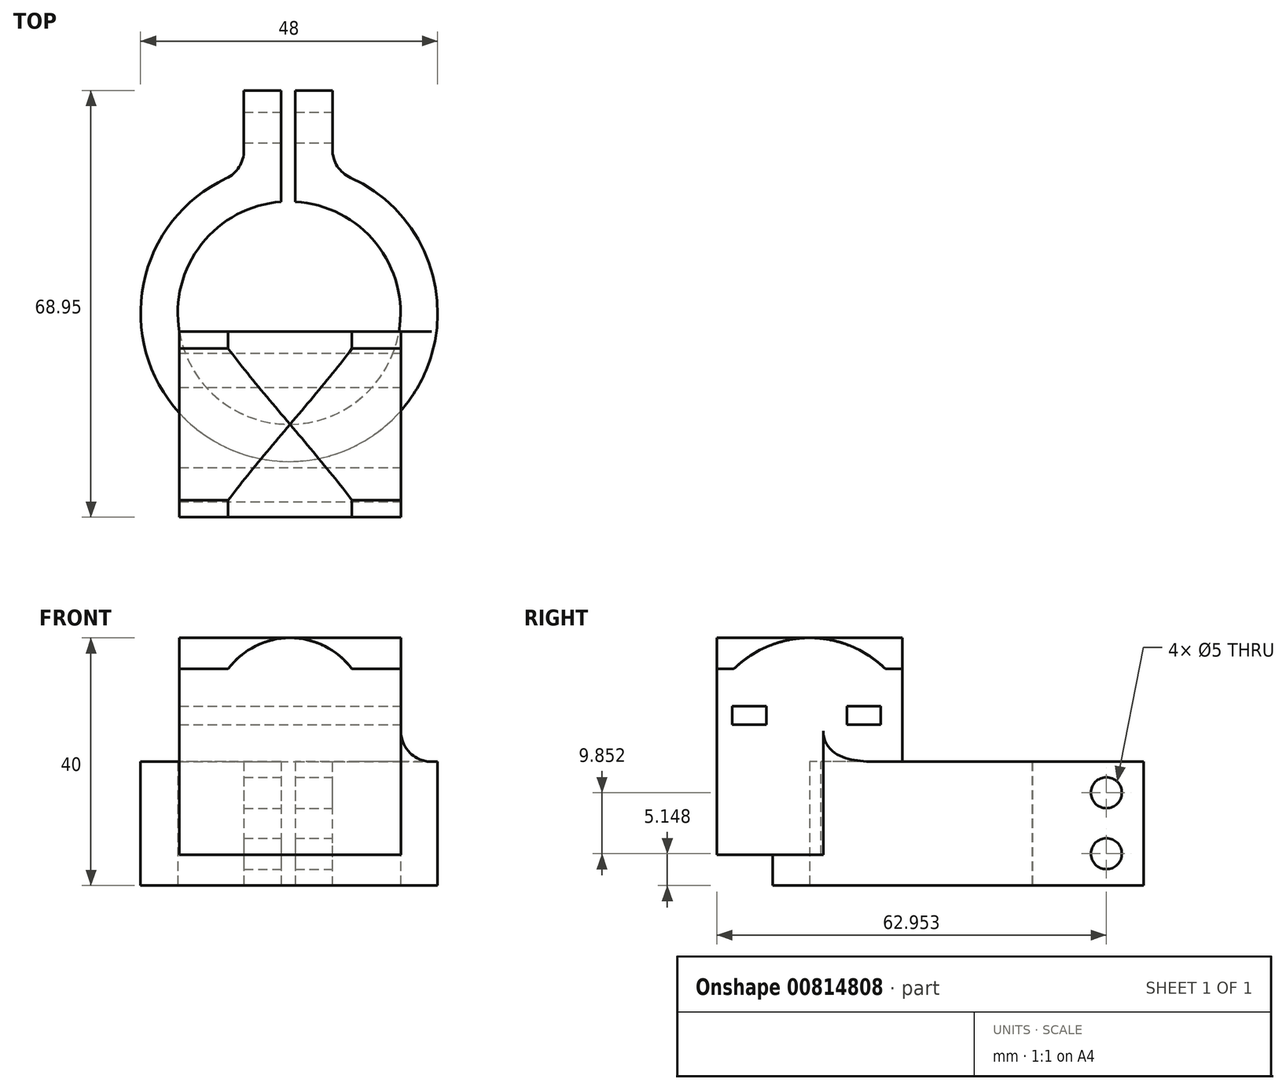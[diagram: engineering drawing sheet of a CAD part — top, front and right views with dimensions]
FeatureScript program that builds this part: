
annotation { "Feature Type Name" : "Feature", "Feature Type Description" : "" }
export const myFeature = defineFeature(function(context is Context, id is Id, definition is map)
    precondition{}
    {
        {
            var Q0;
            Q0=qCreatedBy(makeId("Top.planeOp"),FACE);
            var sketch = newSketch(context, id + "F0", { "sketchPlane" : qUnion([Q0])});
            skArc(sketch, "E0", {"start": v(-1.3, 17.95) * mm, "mid": v(0.15, -18) * mm, "end": v(1, 17.97) * mm});
            skLineSegment(sketch, "E1", {"start": v(-1.3, 17.95) * mm, "end": v(-1.3, 35.95) * mm});
            skLineSegment(sketch, "E2", {"start": v(1, 17.97) * mm, "end": v(1, 35.95) * mm});
            skLineSegment(sketch, "E3.0", {"start": v(7, 22.96) * mm, "end": v(7, 35.95) * mm});
            skArc(sketch, "E3.1", {"start": v(-7.3, 22.86) * mm, "mid": v(0.16, -24) * mm, "end": v(7, 22.96) * mm});
            skLineSegment(sketch, "E3.2", {"start": v(-7.3, 22.86) * mm, "end": v(-7.3, 35.95) * mm});
            skLineSegment(sketch, "E4", {"start": v(-7.3, 35.95) * mm, "end": v(-1.3, 35.95) * mm});
            skLineSegment(sketch, "E5", {"start": v(1, 35.95) * mm, "end": v(7, 35.95) * mm});
            skSolve(sketch);
        }
        {
            var Q0;
            Q0=makeQuery(id+"F0.imprint","IMPRINT",FACE,{"disambiguationData":[TD([[makeQuery(id+"F0.imprint","IMPRINT",EDGE,{"derivedFrom":sQuery(id+"F0.wireOp",EDGE,"E0")}),-1.0]])]});
            extrude(context, id + "F1", {"entities" : qUnion([Q0]), "depth" : 20 * mm, "offsetDistance" : 25 * mm});
        }
        {
            var Q0;
            Q0=makeQuery(id+"F1.opExtrude","SWEPT_EDGE",EDGE,{"disambiguationData":[OSD([sQuery(id+"F0.wireOp",EDGE,"E3.0"),sQuery(id+"F0.wireOp",EDGE,"E3.1")])]});
            var Q1;
            Q1=makeQuery(id+"F1.opExtrude","SWEPT_EDGE",EDGE,{"disambiguationData":[OSD([sQuery(id+"F0.wireOp",EDGE,"E3.1"),sQuery(id+"F0.wireOp",EDGE,"E3.2")])]});
            fillet(context, id + "F2", {"entities" : qUnion([Q0, Q1]), "radius" : 5 * mm, "tangentPropagation" : true, "allowEdgeOverflow" : false});
        }
        {
            var Q0;
            Q0=makeQuery(id+"F1.opExtrude","SWEPT_FACE",FACE,{"disambiguationData":[OSD([sQuery(id+"F0.wireOp",EDGE,"E3.0")])]});
            var sketch = newSketch(context, id + "F3", { "sketchPlane" : qUnion([Q0])});
            skCircle(sketch, "E6", {"center": v(29.95, 15) * mm, "radius": 2.5 * mm});
            skCircle(sketch, "E7", {"center": v(29.95, 5.15) * mm, "radius": 2.5 * mm});
            skSolve(sketch);
        }
        {
            var Q0;
            Q0=makeQuery(id+"F3.imprint","IMPRINT",FACE,{"disambiguationData":[TD([[makeQuery(id+"F3.imprint","IMPRINT",EDGE,{"derivedFrom":sQuery(id+"F3.wireOp",EDGE,"E6")}),1.0]])]});
            var Q1;
            Q1=makeQuery(id+"F3.imprint","IMPRINT",FACE,{"disambiguationData":[TD([[makeQuery(id+"F3.imprint","IMPRINT",EDGE,{"derivedFrom":sQuery(id+"F3.wireOp",EDGE,"E7")}),1.0]])]});
            extrude(context, id + "F4", {"entities" : qUnion([Q0, Q1]), "operationType" : NewBodyOperationType.REMOVE, "oppositeDirection" : true, "depth" : 25 * mm, "offsetDistance" : 25 * mm});
        }
        {
            var Q0;
            Q0=makeQuery(id+"F1.opExtrude","CAP_FACE",FACE,{"disambiguationData":[OSD([sQuery(id+"F0.wireOp",EDGE,"E0"),sQuery(id+"F0.wireOp",EDGE,"E1"),sQuery(id+"F0.wireOp",EDGE,"E2"),sQuery(id+"F0.wireOp",EDGE,"E3.0"),sQuery(id+"F0.wireOp",EDGE,"E3.1"),sQuery(id+"F0.wireOp",EDGE,"E3.2"),sQuery(id+"F0.wireOp",EDGE,"E4"),sQuery(id+"F0.wireOp",EDGE,"E5")])],"isStart":false});
            var sketch = newSketch(context, id + "F5", { "sketchPlane" : qUnion([Q0])});
            skPoint(sketch, "E8.middle", {"position": v(0, 0) * mm});
            skLineSegment(sketch, "E9", {"start": v(-30.55, 0) * mm, "end": v(33.82, 0) * mm, "construction": true});
            skLineSegment(sketch, "E10.bottom", {"start": v(-17.75, -3) * mm, "end": v(18.05, -3) * mm});
            skLineSegment(sketch, "E10.top", {"start": v(-17.75, -33) * mm, "end": v(18.05, -33) * mm});
            skLineSegment(sketch, "E10.left", {"start": v(-17.75, -3) * mm, "end": v(-17.75, -33) * mm});
            skLineSegment(sketch, "E10.right", {"start": v(18.05, -3) * mm, "end": v(18.05, -33) * mm});
            skPoint(sketch, "E10.middle", {"position": v(0.15, -18) * mm});
            skLineSegment(sketch, "E11", {"start": v(0, 0) * mm, "end": v(0, -35.02) * mm, "construction": true});
            skSolve(sketch);
        }
        {
            var Q0;
            {var subQ0=sQuery(id+"F5.wireOp",EDGE,"E10.left");var subQ4=makeQuery(id+"F1.opExtrude","CAP_EDGE",EDGE,{"disambiguationData":[OSD([sQuery(id+"F0.wireOp",EDGE,"E3.1")])],"isStart":false});var subQ5=makeQuery(id+"F5.imprint","INTERSECT",VERTEX,{"derivedFrom":[subQ4,subQ0]});Q0=makeQuery(id+"F5.imprint","IMPRINT",FACE,{"disambiguationData":[TD([[makeQuery(id+"F5.imprint","IMPRINT",EDGE,{"disambiguationData":[TD([[subQ5,-1.0]])],"derivedFrom":subQ4}),1.0]])]});}
            var Q1;
            {var subQ0=sQuery(id+"F5.wireOp",EDGE,"E10.top");Q1=makeQuery(id+"F5.imprint","IMPRINT",FACE,{"disambiguationData":[TD([[makeQuery(id+"F5.imprint","IMPRINT",EDGE,{"derivedFrom":subQ0}),1.0]])]});}
            var Q2;
            {var subQ0=sQuery(id+"F5.wireOp",EDGE,"E10.bottom");Q2=makeQuery(id+"F5.imprint","IMPRINT",FACE,{"disambiguationData":[TD([[makeQuery(id+"F5.imprint","IMPRINT",EDGE,{"derivedFrom":subQ0}),-1.0]])]});}
            extrude(context, id + "F6", {"entities" : qUnion([Q0, Q1, Q2]), "operationType" : NewBodyOperationType.ADD, "depth" : 15 * mm, "offsetDistance" : 25 * mm});
        }
        {
            var Q0;
            {var subQ0=sQuery(id+"F5.wireOp",EDGE,"E10.left");var subQ1=sQuery(id+"F0.wireOp",EDGE,"E3.1");var subQ2=sQuery(id+"F5.wireOp",EDGE,"E10.top");var subQ3=sQuery(id+"F5.wireOp",EDGE,"E10.right");Q0=makeQuery(id+"F6.boolean.opBoolean","SPLIT",FACE,{"disambiguationData":[TD([makeQuery(id+"F1.opExtrude","SWEPT_FACE",FACE,{"disambiguationData":[OSD([subQ1])]})])],"derivedFrom":makeQuery(id+"F6.opExtrude","CAP_FACE",FACE,{"disambiguationData":[OSD([sQuery(id+"F5.wireOp",EDGE,"E10.bottom"),subQ2,subQ0,subQ3])],"isStart":true})});}
            extrude(context, id + "F7", {"entities" : qUnion([Q0]), "operationType" : NewBodyOperationType.ADD, "depth" : 15 * mm, "offsetDistance" : 25 * mm});
        }
        {
            var Q0;
            {var subQ0=sQuery(id+"F5.wireOp",EDGE,"E10.top");Q0=makeQuery(id+"F7.boolean.opBoolean","MERGE",FACE,{"derivedFrom":[makeQuery(id+"F6.opExtrude","SWEPT_FACE",FACE,{"disambiguationData":[OSD([subQ0])]}),makeQuery(id+"F7.opExtrude","SWEPT_FACE",FACE,{"disambiguationData":[OSD([subQ0])]})]});}
            var sketch = newSketch(context, id + "F8", { "sketchPlane" : qUnion([Q0])});
            skCircle(sketch, "E12", {"center": v(0.15, 27.5) * mm, "radius": 12.5 * mm});
            skLineSegment(sketch, "E13", {"start": v(0.15, 5) * mm, "end": v(0.15, 50) * mm, "construction": true});
            skSolve(sketch);
        }
        {
            var Q0;
            {var subQ0=sQuery(id+"F8.wireOp",EDGE,"E12");var subQ1=makeQuery(id+"F6.opExtrude","CAP_EDGE",EDGE,{"disambiguationData":[OSD([sQuery(id+"F5.wireOp",EDGE,"E10.top")])],"isStart":false});var subQ2=makeQuery(id+"F8.imprint","INTERSECT",VERTEX,{"disambiguationData":[OD(0.0)],"derivedFrom":[subQ1,subQ0]});Q0=makeQuery(id+"F8.imprint","IMPRINT",FACE,{"disambiguationData":[TD([[makeQuery(id+"F8.imprint","IMPRINT",EDGE,{"disambiguationData":[TD([[subQ2,1.0]])],"derivedFrom":subQ0}),1.0]])]});}
            extrude(context, id + "F9", {"entities" : qUnion([Q0]), "operationType" : NewBodyOperationType.ADD, "oppositeDirection" : true, "depth" : 30 * mm, "offsetDistance" : 25 * mm});
        }
        {
            var Q0;
            {var subQ0=sQuery(id+"F5.wireOp",EDGE,"E10.right");Q0=makeQuery(id+"F7.boolean.opBoolean","MERGE",FACE,{"derivedFrom":[makeQuery(id+"F6.opExtrude","SWEPT_FACE",FACE,{"disambiguationData":[OSD([subQ0])]}),makeQuery(id+"F7.opExtrude","SWEPT_FACE",FACE,{"disambiguationData":[OSD([subQ0])]})]});}
            var sketch = newSketch(context, id + "F10", { "sketchPlane" : qUnion([Q0])});
            skLineSegment(sketch, "E14", {"start": v(-18, 35) * mm, "end": v(-18, 2.36) * mm, "construction": true});
            skCircle(sketch, "E15", {"center": v(-18, 22.5) * mm, "radius": 17.5 * mm});
            skLineSegment(sketch, "E16.bottom", {"start": v(-25, 26) * mm, "end": v(-30.5, 26) * mm});
            skLineSegment(sketch, "E16.top", {"start": v(-25, 29) * mm, "end": v(-30.5, 29) * mm});
            skLineSegment(sketch, "E16.left", {"start": v(-25, 26) * mm, "end": v(-25, 29) * mm});
            skLineSegment(sketch, "E16.right", {"start": v(-30.5, 26) * mm, "end": v(-30.5, 29) * mm});
            skPoint(sketch, "E16.middle", {"position": v(-27.75, 27.5) * mm});
            skLineSegment(sketch, "E17.bottom", {"start": v(-6.5, 26) * mm, "end": v(-12, 26) * mm});
            skLineSegment(sketch, "E17.top", {"start": v(-6.5, 29) * mm, "end": v(-12, 29) * mm});
            skLineSegment(sketch, "E17.left", {"start": v(-6.5, 26) * mm, "end": v(-6.5, 29) * mm});
            skLineSegment(sketch, "E17.right", {"start": v(-12, 26) * mm, "end": v(-12, 29) * mm});
            skPoint(sketch, "E17.middle", {"position": v(-9.25, 27.5) * mm});
            skSolve(sketch);
        }
        {
            var Q0;
            {var subQ0=sQuery(id+"F10.wireOp",EDGE,"E15");var subQ1=makeQuery(id+"F6.opExtrude","CAP_EDGE",EDGE,{"disambiguationData":[OSD([sQuery(id+"F5.wireOp",EDGE,"E10.right")])],"isStart":false});var subQ2=makeQuery(id+"F10.imprint","INTERSECT",VERTEX,{"disambiguationData":[OD(0.0)],"derivedFrom":[subQ1,subQ0]});Q0=makeQuery(id+"F10.imprint","IMPRINT",FACE,{"disambiguationData":[TD([[makeQuery(id+"F10.imprint","IMPRINT",EDGE,{"disambiguationData":[TD([[subQ2,-1.0]])],"derivedFrom":subQ0}),1.0]])]});}
            extrude(context, id + "F11", {"entities" : qUnion([Q0]), "operationType" : NewBodyOperationType.ADD, "oppositeDirection" : true, "depth" : 35.8 * mm, "offsetDistance" : 25 * mm});
        }
        {
            var Q0;
            Q0=makeQuery(id+"F10.imprint","IMPRINT",FACE,{"disambiguationData":[TD([[makeQuery(id+"F10.imprint","IMPRINT",EDGE,{"derivedFrom":sQuery(id+"F10.wireOp",EDGE,"E16.bottom")}),-1.0]])]});
            var Q1;
            Q1=makeQuery(id+"F10.imprint","IMPRINT",FACE,{"disambiguationData":[TD([[makeQuery(id+"F10.imprint","IMPRINT",EDGE,{"derivedFrom":sQuery(id+"F10.wireOp",EDGE,"E17.bottom")}),-1.0]])]});
            extrude(context, id + "F12", {"entities" : qUnion([Q0, Q1]), "operationType" : NewBodyOperationType.REMOVE, "oppositeDirection" : true, "depth" : 36 * mm, "offsetDistance" : 25 * mm});
        }
        {
            var Q0;
            Q0=makeQuery(id+"F7.opExtrude","CAP_EDGE",EDGE,{"disambiguationData":[OSD([sQuery(id+"F0.wireOp",EDGE,"E3.1")])],"isStart":false});
            var Q1;
            {var subQ0=sQuery(id+"F5.wireOp",EDGE,"E10.right");var subQ1=sQuery(id+"F5.wireOp",EDGE,"E10.left");var subQ2=sQuery(id+"F5.wireOp",EDGE,"E10.top");var subQ3=sQuery(id+"F5.wireOp",EDGE,"E10.bottom");var subQ4=sQuery(id+"F0.wireOp",EDGE,"E3.1");var subQ5=sQuery(id+"F0.wireOp",EDGE,"E5");var subQ6=sQuery(id+"F0.wireOp",EDGE,"E4");var subQ7=sQuery(id+"F0.wireOp",EDGE,"E3.2");var subQ8=sQuery(id+"F0.wireOp",EDGE,"E3.0");var subQ9=sQuery(id+"F0.wireOp",EDGE,"E2");var subQ10=sQuery(id+"F0.wireOp",EDGE,"E1");var subQ11=sQuery(id+"F0.wireOp",EDGE,"E0");Q1=makeQuery(id+"F7.opExtrude","SWEPT_EDGE",EDGE,{"disambiguationData":[OSD([subQ11,subQ10,subQ9,subQ8,subQ4,subQ7,subQ6,subQ5,subQ3,subQ2,subQ1,subQ0]),TDD([makeQuery(id+"F6.boolean.opBoolean","TWEAK_VERTEX",VERTEX,{"derivedFrom":[makeQuery(id+"F1.opExtrude","CAP_FACE",FACE,{"disambiguationData":[OSD([subQ11,subQ10,subQ9,subQ8,subQ4,subQ7,subQ6,subQ5])],"isStart":false}),makeQuery(id+"F1.opExtrude","SWEPT_FACE",FACE,{"disambiguationData":[OSD([subQ4])]}),makeQuery(id+"F6.opExtrude","CAP_FACE",FACE,{"disambiguationData":[OSD([subQ3,subQ2,subQ1,subQ0])],"isStart":true}),makeQuery(id+"F6.opExtrude","SWEPT_FACE",FACE,{"disambiguationData":[OSD([subQ0])]})]})])]});}
            var Q2;
            {var subQ0=sQuery(id+"F5.wireOp",EDGE,"E10.right");Q2=makeQuery(id+"F6.boolean.opBoolean","SPLIT",EDGE,{"disambiguationData":[topologyDisambiguationEdgeConnected([makeQuery(id+"F1.opExtrude","CAP_FACE",FACE,{"disambiguationData":[OSD([sQuery(id+"F0.wireOp",EDGE,"E0"),sQuery(id+"F0.wireOp",EDGE,"E1"),sQuery(id+"F0.wireOp",EDGE,"E2"),sQuery(id+"F0.wireOp",EDGE,"E3.0"),sQuery(id+"F0.wireOp",EDGE,"E3.1"),sQuery(id+"F0.wireOp",EDGE,"E3.2"),sQuery(id+"F0.wireOp",EDGE,"E4"),sQuery(id+"F0.wireOp",EDGE,"E5")])],"isStart":false})])],"derivedFrom":makeQuery(id+"F6.opExtrude","CAP_EDGE",EDGE,{"disambiguationData":[OSD([subQ0])],"isStart":true})});}
            var Q3;
            {var subQ0=sQuery(id+"F5.wireOp",EDGE,"E10.left");Q3=makeQuery(id+"F6.boolean.opBoolean","SPLIT",EDGE,{"disambiguationData":[topologyDisambiguationEdgeConnected([makeQuery(id+"F1.opExtrude","CAP_FACE",FACE,{"disambiguationData":[OSD([sQuery(id+"F0.wireOp",EDGE,"E0"),sQuery(id+"F0.wireOp",EDGE,"E1"),sQuery(id+"F0.wireOp",EDGE,"E2"),sQuery(id+"F0.wireOp",EDGE,"E3.0"),sQuery(id+"F0.wireOp",EDGE,"E3.1"),sQuery(id+"F0.wireOp",EDGE,"E3.2"),sQuery(id+"F0.wireOp",EDGE,"E4"),sQuery(id+"F0.wireOp",EDGE,"E5")])],"isStart":false})])],"derivedFrom":makeQuery(id+"F6.opExtrude","CAP_EDGE",EDGE,{"disambiguationData":[OSD([subQ0])],"isStart":true})});}
            var Q4;
            {var subQ0=sQuery(id+"F5.wireOp",EDGE,"E10.left");var subQ1=sQuery(id+"F5.wireOp",EDGE,"E10.right");var subQ2=sQuery(id+"F5.wireOp",EDGE,"E10.top");var subQ3=sQuery(id+"F5.wireOp",EDGE,"E10.bottom");var subQ4=sQuery(id+"F0.wireOp",EDGE,"E3.1");var subQ5=sQuery(id+"F0.wireOp",EDGE,"E5");var subQ6=sQuery(id+"F0.wireOp",EDGE,"E4");var subQ7=sQuery(id+"F0.wireOp",EDGE,"E3.2");var subQ8=sQuery(id+"F0.wireOp",EDGE,"E3.0");var subQ9=sQuery(id+"F0.wireOp",EDGE,"E2");var subQ10=sQuery(id+"F0.wireOp",EDGE,"E1");var subQ11=sQuery(id+"F0.wireOp",EDGE,"E0");Q4=makeQuery(id+"F7.opExtrude","SWEPT_EDGE",EDGE,{"disambiguationData":[OSD([subQ11,subQ10,subQ9,subQ8,subQ4,subQ7,subQ6,subQ5,subQ3,subQ2,subQ0,subQ1]),TDD([makeQuery(id+"F6.boolean.opBoolean","TWEAK_VERTEX",VERTEX,{"derivedFrom":[makeQuery(id+"F1.opExtrude","CAP_FACE",FACE,{"disambiguationData":[OSD([subQ11,subQ10,subQ9,subQ8,subQ4,subQ7,subQ6,subQ5])],"isStart":false}),makeQuery(id+"F1.opExtrude","SWEPT_FACE",FACE,{"disambiguationData":[OSD([subQ4])]}),makeQuery(id+"F6.opExtrude","CAP_FACE",FACE,{"disambiguationData":[OSD([subQ3,subQ2,subQ0,subQ1])],"isStart":true}),makeQuery(id+"F6.opExtrude","SWEPT_FACE",FACE,{"disambiguationData":[OSD([subQ0])]})]})])]});}
            fillet(context, id + "F13", {"entities" : qUnion([Q0, Q1, Q2, Q3, Q4]), "radius" : 5 * mm, "tangentPropagation" : true, "allowEdgeOverflow" : false});
        }
    });
